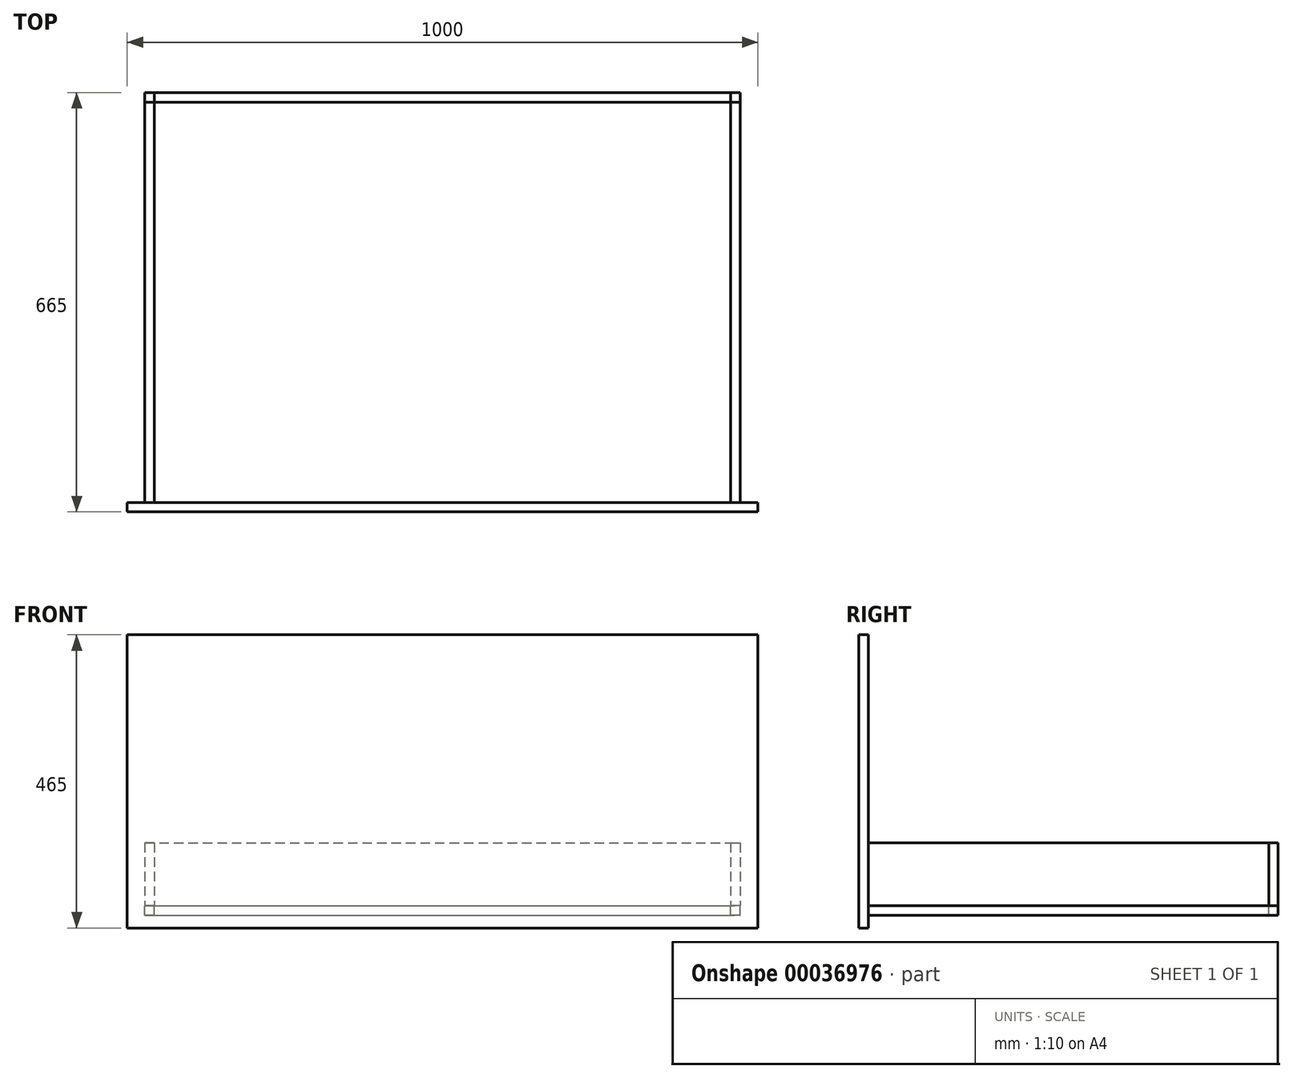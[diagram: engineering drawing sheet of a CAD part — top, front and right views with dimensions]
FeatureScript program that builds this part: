
annotation { "Feature Type Name" : "Feature", "Feature Type Description" : "" }
export const myFeature = defineFeature(function(context is Context, id is Id, definition is map)
    precondition{}
    {
        {
            var Q0;
            Q0=qCreatedBy(makeId("Top.planeOp"),FACE);
            var sketch = newSketch(context, id + "F0", { "sketchPlane" : qUnion([Q0])});
            skLineSegment(sketch, "E0.rect.bottom", {"start": v(500, -7.5) * mm, "end": v(-500, -7.5) * mm});
            skLineSegment(sketch, "E0.rect.top", {"start": v(500, 7.5) * mm, "end": v(-500, 7.5) * mm});
            skLineSegment(sketch, "E0.rect.left", {"start": v(500, -7.5) * mm, "end": v(500, 7.5) * mm});
            skLineSegment(sketch, "E0.rect.right", {"start": v(-500, -7.5) * mm, "end": v(-500, 7.5) * mm});
            skPoint(sketch, "E0.rect.middle", {"position": v(0, 0) * mm});
            skLineSegment(sketch, "E1.rect.bottom", {"start": v(472, 7.5) * mm, "end": v(-472, 7.5) * mm});
            skLineSegment(sketch, "E1.rect.top", {"start": v(472, 7.5) * mm, "end": v(-472, 7.5) * mm});
            skLineSegment(sketch, "E1.rect.left", {"start": v(472, 7.5) * mm, "end": v(472, 7.5) * mm});
            skLineSegment(sketch, "E1.rect.right", {"start": v(-472, 7.5) * mm, "end": v(-472, 7.5) * mm});
            skPoint(sketch, "E1.rect.middle", {"position": v(0, 7.5) * mm});
            skLineSegment(sketch, "E2.bottom", {"start": v(-472, 7.5) * mm, "end": v(472, 7.5) * mm});
            skLineSegment(sketch, "E2.top", {"start": v(-472, 657.5) * mm, "end": v(472, 657.5) * mm});
            skLineSegment(sketch, "E2.left", {"start": v(-472, 7.5) * mm, "end": v(-472, 657.5) * mm});
            skLineSegment(sketch, "E2.right", {"start": v(472, 7.5) * mm, "end": v(472, 657.5) * mm});
            skLineSegment(sketch, "E3.0", {"start": v(457, 7.5) * mm, "end": v(457, 657.5) * mm});
            skLineSegment(sketch, "E4.0", {"start": v(-457, 7.5) * mm, "end": v(-457, 657.5) * mm});
            skLineSegment(sketch, "E5.0", {"start": v(-472, 642.5) * mm, "end": v(472, 642.5) * mm});
            skSolve(sketch);
        }
        {
            var Q0;
            {var subQ3=sQuery(id+"F0.wireOp",EDGE,"E3.0");var subQ5=sQuery(id+"F0.wireOp",EDGE,"E2.top");var subQ7=makeQuery(id+"F0.imprint","INTERSECT",VERTEX,{"derivedFrom":[subQ5,subQ3]});Q0=makeQuery(id+"F0.imprint","IMPRINT",FACE,{"disambiguationData":[TD([[makeQuery(id+"F0.imprint","IMPRINT",EDGE,{"disambiguationData":[TD([[subQ7,1.0]])],"derivedFrom":subQ5}),-1.0]])]});}
            var Q1;
            {var subQ3=sQuery(id+"F0.wireOp",EDGE,"E2.top");var subQ5=sQuery(id+"F0.wireOp",EDGE,"E2.right");var subQ7=makeQuery(id+"F0.imprint","INTERSECT",VERTEX,{"derivedFrom":[subQ3,subQ5]});Q1=makeQuery(id+"F0.imprint","IMPRINT",FACE,{"disambiguationData":[TD([[makeQuery(id+"F0.imprint","IMPRINT",EDGE,{"disambiguationData":[TD([[subQ7,1.0]])],"derivedFrom":subQ3}),-1.0]])]});}
            var Q2;
            {var subQ3=sQuery(id+"F0.wireOp",EDGE,"E2.top");var subQ5=sQuery(id+"F0.wireOp",EDGE,"E2.left");var subQ7=makeQuery(id+"F0.imprint","INTERSECT",VERTEX,{"derivedFrom":[subQ3,subQ5]});Q2=makeQuery(id+"F0.imprint","IMPRINT",FACE,{"disambiguationData":[TD([[makeQuery(id+"F0.imprint","IMPRINT",EDGE,{"disambiguationData":[TD([[subQ7,-1.0]])],"derivedFrom":subQ3}),-1.0]])]});}
            extrude(context, id + "F1", {"entities" : qUnion([Q0, Q1, Q2]), "depth" : 100 * mm});
        }
        {
            var Q0;
            {var subQ1=sQuery(id+"F0.wireOp",EDGE,"E3.0");var subQ5=sQuery(id+"F0.wireOp",EDGE,"E2.bottom");var subQ6=makeQuery(id+"F0.imprint","INTERSECT",VERTEX,{"derivedFrom":[subQ5,subQ1]});Q0=makeQuery(id+"F0.imprint","IMPRINT",FACE,{"disambiguationData":[TD([[makeQuery(id+"F0.imprint","IMPRINT",EDGE,{"disambiguationData":[TD([[subQ6,-1.0]])],"derivedFrom":subQ1}),-1.0]])]});}
            extrude(context, id + "F2", {"entities" : qUnion([Q0]), "depth" : 100 * mm});
        }
        {
            var Q0;
            {var subQ1=sQuery(id+"F0.wireOp",EDGE,"E4.0");var subQ5=sQuery(id+"F0.wireOp",EDGE,"E2.bottom");var subQ6=makeQuery(id+"F0.imprint","INTERSECT",VERTEX,{"derivedFrom":[subQ5,subQ1]});Q0=makeQuery(id+"F0.imprint","IMPRINT",FACE,{"disambiguationData":[TD([[makeQuery(id+"F0.imprint","IMPRINT",EDGE,{"disambiguationData":[TD([[subQ6,-1.0]])],"derivedFrom":subQ1}),1.0]])]});}
            extrude(context, id + "F3", {"entities" : qUnion([Q0]), "depth" : 100 * mm});
        }
        {
            var Q0;
            Q0=makeQuery(id+"F0.imprint","IMPRINT",FACE,{"disambiguationData":[TD([[makeQuery(id+"F0.imprint","IMPRINT",EDGE,{"derivedFrom":sQuery(id+"F0.wireOp",EDGE,"E0.rect.bottom")}),-1.0]])]});
            extrude(context, id + "F4", {"entities" : qUnion([Q0]), "depth" : 430 * mm, "hasSecondDirection" : true, "secondDirectionOppositeDirection" : true, "secondDirectionDepth" : 35 * mm});
        }
        {
            var Q0;
            {var subQ1=sQuery(id+"F0.wireOp",EDGE,"E3.0");var subQ5=sQuery(id+"F0.wireOp",EDGE,"E2.bottom");var subQ6=makeQuery(id+"F0.imprint","INTERSECT",VERTEX,{"derivedFrom":[subQ5,subQ1]});Q0=makeQuery(id+"F0.imprint","IMPRINT",FACE,{"disambiguationData":[TD([[makeQuery(id+"F0.imprint","IMPRINT",EDGE,{"disambiguationData":[TD([[subQ6,-1.0]])],"derivedFrom":subQ1}),-1.0]])]});}
            var Q1;
            {var subQ3=sQuery(id+"F0.wireOp",EDGE,"E3.0");var subQ5=sQuery(id+"F0.wireOp",EDGE,"E2.bottom");var subQ7=makeQuery(id+"F0.imprint","INTERSECT",VERTEX,{"derivedFrom":[subQ5,subQ3]});Q1=makeQuery(id+"F0.imprint","IMPRINT",FACE,{"disambiguationData":[TD([[makeQuery(id+"F0.imprint","IMPRINT",EDGE,{"disambiguationData":[TD([[subQ7,1.0]])],"derivedFrom":subQ5}),1.0]])]});}
            var Q2;
            {var subQ3=sQuery(id+"F0.wireOp",EDGE,"E3.0");var subQ5=sQuery(id+"F0.wireOp",EDGE,"E2.top");var subQ7=makeQuery(id+"F0.imprint","INTERSECT",VERTEX,{"derivedFrom":[subQ5,subQ3]});Q2=makeQuery(id+"F0.imprint","IMPRINT",FACE,{"disambiguationData":[TD([[makeQuery(id+"F0.imprint","IMPRINT",EDGE,{"disambiguationData":[TD([[subQ7,1.0]])],"derivedFrom":subQ5}),-1.0]])]});}
            var Q3;
            {var subQ1=sQuery(id+"F0.wireOp",EDGE,"E4.0");var subQ5=sQuery(id+"F0.wireOp",EDGE,"E2.bottom");var subQ6=makeQuery(id+"F0.imprint","INTERSECT",VERTEX,{"derivedFrom":[subQ5,subQ1]});Q3=makeQuery(id+"F0.imprint","IMPRINT",FACE,{"disambiguationData":[TD([[makeQuery(id+"F0.imprint","IMPRINT",EDGE,{"disambiguationData":[TD([[subQ6,-1.0]])],"derivedFrom":subQ1}),1.0]])]});}
            var Q4;
            {var subQ3=sQuery(id+"F0.wireOp",EDGE,"E2.top");var subQ5=sQuery(id+"F0.wireOp",EDGE,"E2.right");var subQ7=makeQuery(id+"F0.imprint","INTERSECT",VERTEX,{"derivedFrom":[subQ3,subQ5]});Q4=makeQuery(id+"F0.imprint","IMPRINT",FACE,{"disambiguationData":[TD([[makeQuery(id+"F0.imprint","IMPRINT",EDGE,{"disambiguationData":[TD([[subQ7,1.0]])],"derivedFrom":subQ3}),-1.0]])]});}
            var Q5;
            {var subQ3=sQuery(id+"F0.wireOp",EDGE,"E2.top");var subQ5=sQuery(id+"F0.wireOp",EDGE,"E2.left");var subQ7=makeQuery(id+"F0.imprint","INTERSECT",VERTEX,{"derivedFrom":[subQ3,subQ5]});Q5=makeQuery(id+"F0.imprint","IMPRINT",FACE,{"disambiguationData":[TD([[makeQuery(id+"F0.imprint","IMPRINT",EDGE,{"disambiguationData":[TD([[subQ7,-1.0]])],"derivedFrom":subQ3}),-1.0]])]});}
            extrude(context, id + "F5", {"entities" : qUnion([Q0, Q1, Q2, Q3, Q4, Q5]), "oppositeDirection" : true, "depth" : 15 * mm});
        }
    });
